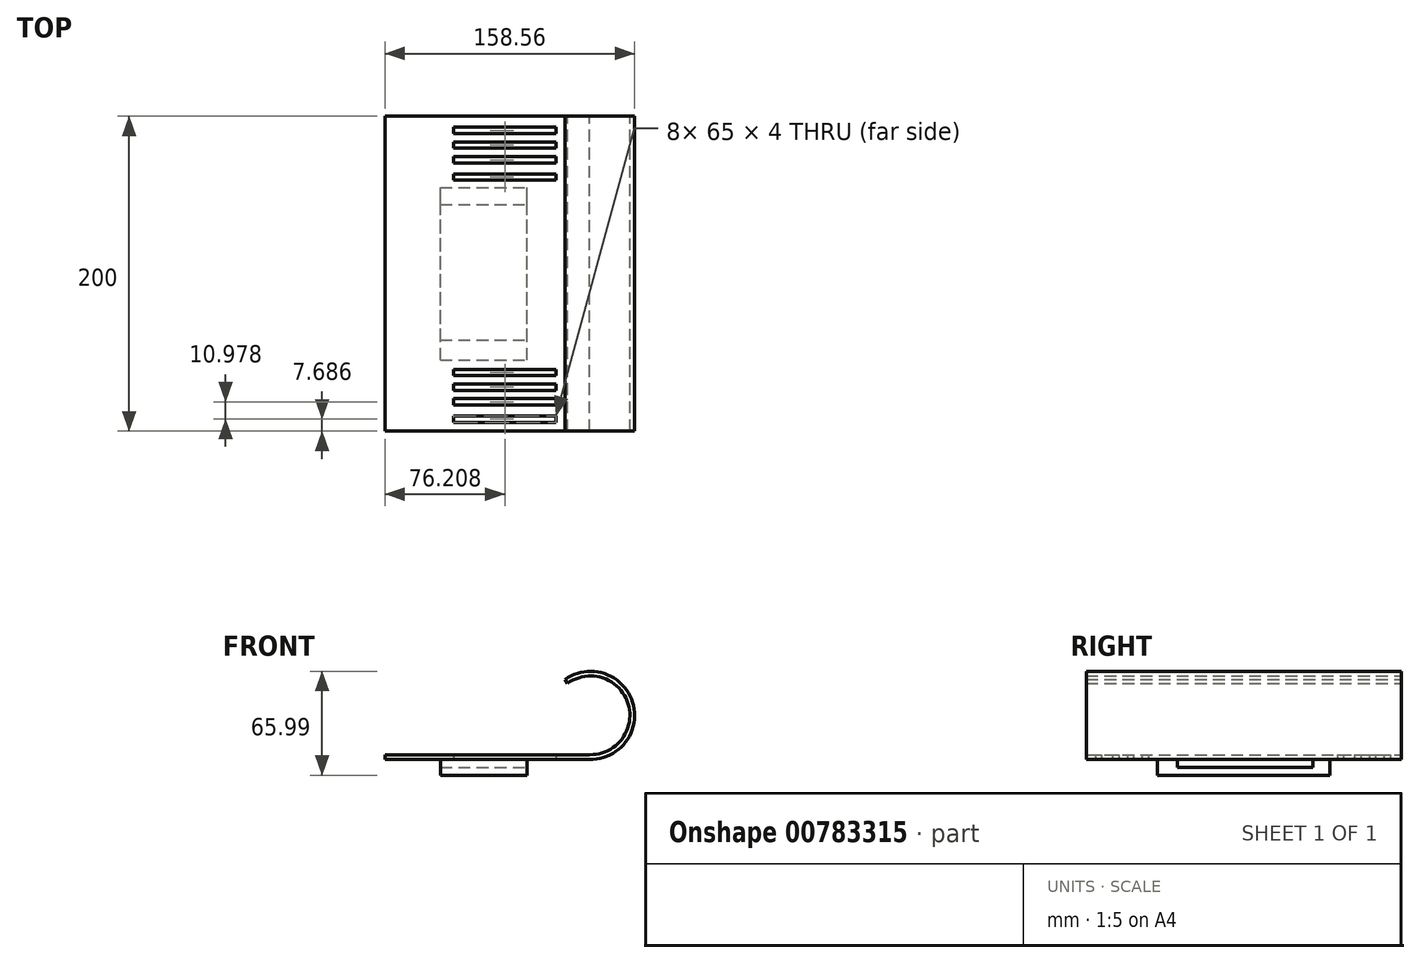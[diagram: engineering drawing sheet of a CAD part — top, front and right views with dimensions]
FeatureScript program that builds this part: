
annotation { "Feature Type Name" : "Feature", "Feature Type Description" : "" }
export const myFeature = defineFeature(function(context is Context, id is Id, definition is map)
    precondition{}
    {
        {
            var Q0;
            Q0=qCreatedBy(makeId("Front.planeOp"),FACE);
            var sketch = newSketch(context, id + "F0", { "sketchPlane" : qUnion([Q0])});
            skLineSegment(sketch, "E0", {"start": v(54.47, 0) * mm, "end": v(-75.53, 0) * mm});
            skArc(sketch, "E1", {"start": v(54.47, 0) * mm, "mid": v(78.92, 32.36) * mm, "end": v(40.48, 45.33) * mm});
            skPoint(sketch, "E2", {"position": v(40.48, 45.33) * mm});
            skLineSegment(sketch, "E3.0", {"start": v(54.43, -3) * mm, "end": v(-75.52, -3) * mm});
            skArc(sketch, "E3.1", {"start": v(54.43, -3) * mm, "mid": v(81.78, 33.26) * mm, "end": v(38.74, 47.77) * mm});
            skLineSegment(sketch, "E4", {"start": v(40.48, 45.33) * mm, "end": v(38.74, 47.77) * mm});
            skLineSegment(sketch, "E5", {"start": v(-75.52, -3) * mm, "end": v(-75.53, 0) * mm});
            skSolve(sketch);
        }
        {
            var Q0;
            Q0=makeQuery(id+"F0.imprint","IMPRINT",FACE,{"disambiguationData":[TD([[makeQuery(id+"F0.imprint","IMPRINT",EDGE,{"derivedFrom":sQuery(id+"F0.wireOp",EDGE,"E0")}),1.0]])]});
            extrude(context, id + "F1", {"entities" : qUnion([Q0]), "depth" : 200 * mm, "offsetDistance" : 25 * mm});
        }
        {
            var Q0;
            Q0=makeQuery(id+"F1.opExtrude","SWEPT_FACE",FACE,{"disambiguationData":[OSD([sQuery(id+"F0.wireOp",EDGE,"E3.0")])]});
            var sketch = newSketch(context, id + "F2", { "sketchPlane" : qUnion([Q0])});
            skLineSegment(sketch, "E6.bottom", {"start": v(-40.33, 154.81) * mm, "end": v(14.67, 154.81) * mm});
            skLineSegment(sketch, "E6.top", {"start": v(-40.33, 45.37) * mm, "end": v(14.67, 45.37) * mm});
            skLineSegment(sketch, "E6.left", {"start": v(-40.33, 154.81) * mm, "end": v(-40.33, 45.37) * mm});
            skLineSegment(sketch, "E6.right", {"start": v(14.67, 154.81) * mm, "end": v(14.67, 45.37) * mm});
            skSolve(sketch);
        }
        {
            var Q0;
            Q0=makeQuery(id+"F2.imprint","IMPRINT",FACE,{"disambiguationData":[TD([[makeQuery(id+"F2.imprint","IMPRINT",EDGE,{"derivedFrom":sQuery(id+"F2.wireOp",EDGE,"E6.bottom")}),-1.0]])]});
            extrude(context, id + "F3", {"entities" : qUnion([Q0]), "operationType" : NewBodyOperationType.ADD, "depth" : 10 * mm, "offsetDistance" : 25 * mm});
        }
        {
            var Q0;
            Q0=makeQuery(id+"F3.opExtrude","SWEPT_FACE",FACE,{"disambiguationData":[OSD([sQuery(id+"F2.wireOp",EDGE,"E6.right")])]});
            var sketch = newSketch(context, id + "F4", { "sketchPlane" : qUnion([Q0])});
            skLineSegment(sketch, "E7.bottom", {"start": v(-142.17, -3) * mm, "end": v(-56.01, -3) * mm});
            skLineSegment(sketch, "E7.top", {"start": v(-142.17, -8.17) * mm, "end": v(-56.01, -8.17) * mm});
            skLineSegment(sketch, "E7.left", {"start": v(-142.17, -3) * mm, "end": v(-142.17, -8.17) * mm});
            skLineSegment(sketch, "E7.right", {"start": v(-56.01, -3) * mm, "end": v(-56.01, -8.17) * mm});
            skSolve(sketch);
        }
        {
            var Q0;
            Q0=makeQuery(id+"F4.imprint","IMPRINT",FACE,{"disambiguationData":[TD([[makeQuery(id+"F4.imprint","IMPRINT",EDGE,{"derivedFrom":sQuery(id+"F4.wireOp",EDGE,"E7.bottom")}),-1.0]])]});
            extrude(context, id + "F5", {"entities" : qUnion([Q0]), "operationType" : NewBodyOperationType.REMOVE, "oppositeDirection" : true, "depth" : 56 * mm, "offsetDistance" : 25 * mm});
        }
        {
            var Q0;
            Q0=makeQuery(id+"F5.boolean.opBoolean","MERGE",FACE,{"derivedFrom":[makeQuery(id+"F1.opExtrude","SWEPT_FACE",FACE,{"disambiguationData":[OSD([sQuery(id+"F0.wireOp",EDGE,"E3.0")])]}),makeQuery(id+"F5.opExtrude","SWEPT_FACE",FACE,{"disambiguationData":[OSD([sQuery(id+"F4.wireOp",EDGE,"E7.bottom")])]})]});
            var sketch = newSketch(context, id + "F6", { "sketchPlane" : qUnion([Q0])});
            skLineSegment(sketch, "E8.bottom", {"start": v(33.18, 194.31) * mm, "end": v(-31.82, 194.31) * mm});
            skLineSegment(sketch, "E8.top", {"start": v(33.18, 190.31) * mm, "end": v(-31.82, 190.31) * mm});
            skLineSegment(sketch, "E8.left", {"start": v(33.18, 194.31) * mm, "end": v(33.18, 190.31) * mm});
            skLineSegment(sketch, "E8.right", {"start": v(-31.82, 194.31) * mm, "end": v(-31.82, 190.31) * mm});
            skLineSegment(sketch, "E9.bottom", {"start": v(33.18, 183.34) * mm, "end": v(-31.82, 183.34) * mm});
            skLineSegment(sketch, "E9.top", {"start": v(33.18, 179.34) * mm, "end": v(-31.82, 179.34) * mm});
            skLineSegment(sketch, "E9.left", {"start": v(33.18, 183.34) * mm, "end": v(33.18, 179.34) * mm});
            skLineSegment(sketch, "E9.right", {"start": v(-31.82, 183.34) * mm, "end": v(-31.82, 179.34) * mm});
            skLineSegment(sketch, "E10.bottom", {"start": v(33.18, 174) * mm, "end": v(-31.82, 174) * mm});
            skLineSegment(sketch, "E10.top", {"start": v(33.18, 170) * mm, "end": v(-31.82, 170) * mm});
            skLineSegment(sketch, "E10.left", {"start": v(33.18, 174) * mm, "end": v(33.18, 170) * mm});
            skLineSegment(sketch, "E10.right", {"start": v(-31.82, 174) * mm, "end": v(-31.82, 170) * mm});
            skLineSegment(sketch, "E11.bottom", {"start": v(33.18, 164.68) * mm, "end": v(-31.82, 164.68) * mm});
            skLineSegment(sketch, "E11.top", {"start": v(33.18, 160.68) * mm, "end": v(-31.82, 160.68) * mm});
            skLineSegment(sketch, "E11.left", {"start": v(33.18, 164.68) * mm, "end": v(33.18, 160.68) * mm});
            skLineSegment(sketch, "E11.right", {"start": v(-31.82, 164.68) * mm, "end": v(-31.82, 160.68) * mm});
            skLineSegment(sketch, "E12.bottom", {"start": v(33.18, 40.6) * mm, "end": v(-31.82, 40.6) * mm});
            skLineSegment(sketch, "E12.top", {"start": v(33.18, 36.6) * mm, "end": v(-31.82, 36.6) * mm});
            skLineSegment(sketch, "E12.left", {"start": v(33.18, 40.6) * mm, "end": v(33.18, 36.6) * mm});
            skLineSegment(sketch, "E12.right", {"start": v(-31.82, 40.6) * mm, "end": v(-31.82, 36.6) * mm});
            skLineSegment(sketch, "E13.bottom", {"start": v(33.18, 29.63) * mm, "end": v(-31.82, 29.63) * mm});
            skLineSegment(sketch, "E13.top", {"start": v(33.18, 25.63) * mm, "end": v(-31.82, 25.63) * mm});
            skLineSegment(sketch, "E13.left", {"start": v(33.18, 29.63) * mm, "end": v(33.18, 25.63) * mm});
            skLineSegment(sketch, "E13.right", {"start": v(-31.82, 29.63) * mm, "end": v(-31.82, 25.63) * mm});
            skLineSegment(sketch, "E14.bottom", {"start": v(33.18, 20.29) * mm, "end": v(-31.82, 20.29) * mm});
            skLineSegment(sketch, "E14.top", {"start": v(33.18, 16.29) * mm, "end": v(-31.82, 16.29) * mm});
            skLineSegment(sketch, "E14.left", {"start": v(33.18, 20.29) * mm, "end": v(33.18, 16.29) * mm});
            skLineSegment(sketch, "E14.right", {"start": v(-31.82, 20.29) * mm, "end": v(-31.82, 16.29) * mm});
            skLineSegment(sketch, "E15.bottom", {"start": v(33.18, 10.97) * mm, "end": v(-31.82, 10.97) * mm});
            skLineSegment(sketch, "E15.top", {"start": v(33.18, 6.97) * mm, "end": v(-31.82, 6.97) * mm});
            skLineSegment(sketch, "E15.left", {"start": v(33.18, 10.97) * mm, "end": v(33.18, 6.97) * mm});
            skLineSegment(sketch, "E15.right", {"start": v(-31.82, 10.97) * mm, "end": v(-31.82, 6.97) * mm});
            skSolve(sketch);
        }
        {
            var Q0;
            Q0=makeQuery(id+"F6.imprint","IMPRINT",FACE,{"disambiguationData":[TD([[makeQuery(id+"F6.imprint","IMPRINT",EDGE,{"derivedFrom":sQuery(id+"F6.wireOp",EDGE,"E9.bottom")}),1.0]])]});
            var Q1;
            Q1=makeQuery(id+"F6.imprint","IMPRINT",FACE,{"disambiguationData":[TD([[makeQuery(id+"F6.imprint","IMPRINT",EDGE,{"derivedFrom":sQuery(id+"F6.wireOp",EDGE,"E10.bottom")}),1.0]])]});
            var Q2;
            Q2=makeQuery(id+"F6.imprint","IMPRINT",FACE,{"disambiguationData":[TD([[makeQuery(id+"F6.imprint","IMPRINT",EDGE,{"derivedFrom":sQuery(id+"F6.wireOp",EDGE,"E11.bottom")}),1.0]])]});
            var Q3;
            Q3=makeQuery(id+"F6.imprint","IMPRINT",FACE,{"disambiguationData":[TD([[makeQuery(id+"F6.imprint","IMPRINT",EDGE,{"derivedFrom":sQuery(id+"F6.wireOp",EDGE,"E12.bottom")}),1.0]])]});
            var Q4;
            Q4=makeQuery(id+"F6.imprint","IMPRINT",FACE,{"disambiguationData":[TD([[makeQuery(id+"F6.imprint","IMPRINT",EDGE,{"derivedFrom":sQuery(id+"F6.wireOp",EDGE,"E13.bottom")}),1.0]])]});
            var Q5;
            Q5=makeQuery(id+"F6.imprint","IMPRINT",FACE,{"disambiguationData":[TD([[makeQuery(id+"F6.imprint","IMPRINT",EDGE,{"derivedFrom":sQuery(id+"F6.wireOp",EDGE,"E14.bottom")}),1.0]])]});
            var Q6;
            Q6=makeQuery(id+"F6.imprint","IMPRINT",FACE,{"disambiguationData":[TD([[makeQuery(id+"F6.imprint","IMPRINT",EDGE,{"derivedFrom":sQuery(id+"F6.wireOp",EDGE,"E15.bottom")}),1.0]])]});
            var Q7;
            Q7=makeQuery(id+"F6.imprint","IMPRINT",FACE,{"disambiguationData":[TD([[makeQuery(id+"F6.imprint","IMPRINT",EDGE,{"derivedFrom":sQuery(id+"F6.wireOp",EDGE,"E8.bottom")}),1.0]])]});
            extrude(context, id + "F7", {"entities" : qUnion([Q0, Q1, Q2, Q3, Q4, Q5, Q6, Q7]), "operationType" : NewBodyOperationType.REMOVE, "oppositeDirection" : true, "depth" : 16 * mm, "offsetDistance" : 25 * mm});
        }
    });
